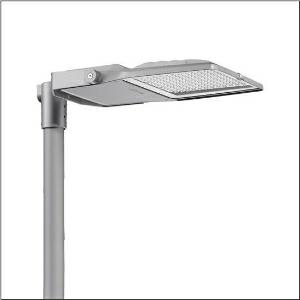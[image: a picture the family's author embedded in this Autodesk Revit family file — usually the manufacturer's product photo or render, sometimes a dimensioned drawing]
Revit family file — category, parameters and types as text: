
# Revit family: floodlight_fl_21_midi___pl61_5xa7786e2c3a_519c
name_source: partatom
category: Lighting Fixtures
units: mm (PartAtom-declared; Revit-internal decimal feet)

## family parameters
Cut with Voids When Loaded = No
Host = Face
Light Source = No
Part Type = Normal
Room Calculation Point = No
Round Connector Dimension = Use Diameter
Shared = No

## types (1)
- --- (1 x LED, 26450 lm, 212.4 W, 3000K)
    Apparent Load = 212 VA
    CIE Flux Codes = 33 65 98 100 100
    Color Rendering = 70
    Color Temperature = 3000K
    Default Elevation = 1800 mm
    Description = Floodlight FL 21 midi, floodlight, primary light control with lens, of PMMA, primary optical cover: protective disc, of toughened safety glass, transparent, light distribution: PL61, light emission: direct distribution, installation type: surface-mounted, LED, High Power LED, rated luminous flux: 26.450lm, luminous efficacy: 125lm/W, light colour: 730, colour temperature: 3000K, control gear: Smart Interface (Zhaga), control: flexible luminous flux parameterisation, time-dependent luminous flux control, constant luminous flux control, overheat protection, pre-setting: logarithmic dimming characteristic, with terminal, 6-pole, mains connection: 220..240V, AC, 50/60Hz, start of lifetime: 212W, end of service life: 231W, reduction: 95W, luminaire housing, of diecast aluminium, powder-coated, Siteco® metallic grey (DB 702S), corrosivity category C5 mid according to DIN EN ISO 12944, suitable for swimming pools, chlorine-resistant, sealing non-destructively replaceable, please order mast flange separately, mast bracket, of steel, galvanised, powder-coated, Siteco® metallic grey (DB 702S), Smart Interface below and above, protection rating (complete): IP66, insulation class (complete): insulation class II (safety insulation), certification: CE, ENEC, VDE, protection symbol: D, impact resistance: IK08, permissible operating ambient temperature: -40..+40°C, permissible operating ambient temperature for outdoor applications: -40..+50°C, standard: DIN EN 12944, LABS conformity tested according to VDMA 24364:2018-05, packaging unit: 1 piece

Light Distribution: PL61
    Height = 76 mm
    Lamp = 1 x LED
    Lamp Light Flux = 26450 lm
    Lamp Power = 212.4 W
    Lamp count = 1
    Length = 657 mm
    Luminous efficacy = 125 lm/W
    Manufacturer = Siteco
    ModVariant = No
    Model = 5XA7786E2C3A
    Number of Poles = 1
    OnlyDefault = Yes
    Power Factor = 1
    Product Name = Floodlight FL 21 midi | PL61
    Product group = floodlight | pylon annexe
    ProductGroupID = 6200
    Protection Class = Protection class II
    Protection Degree = IP 66
    RLX_Detail_Level = 1
    RLX_Emergency_Light_Flux = 0 lm
    RLX_Emergency_Type = 0
    RLX_Emergency_Type_DB = No
    RlxData = <blob elided: 153881 chars, md5=26b6137f>
    Socket = socket
    Standby Power = 0 W
    System Light Flux = 26450 lm
    System Power = 212 W
    Type Comments = factory setting: luminous flux: 100 % | dim-lin: 254 | 710 mA
    Type Image = l_1007123.jpg
    URL = http://relux.com
    VarID = @adj_194076
    Voltage = 0 V
    Weight = 0.00 kg
    Width = 442 mm

## geometry (parser evidence)
native form markers: Blend x4, Sweep x13
no freeform markers — native parametric forms only
